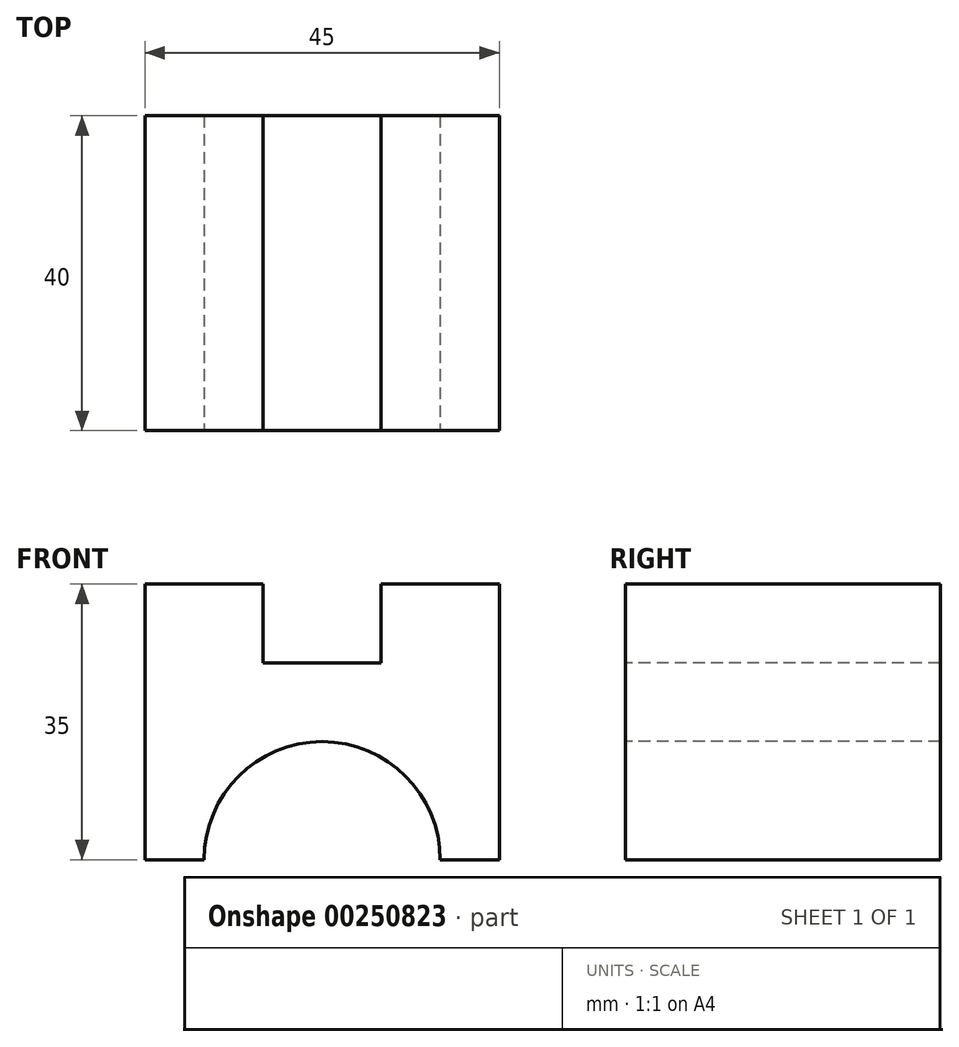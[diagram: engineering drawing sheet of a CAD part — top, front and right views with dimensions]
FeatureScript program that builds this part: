
annotation { "Feature Type Name" : "Feature", "Feature Type Description" : "" }
export const myFeature = defineFeature(function(context is Context, id is Id, definition is map)
    precondition{}
    {
        {
            var Q0;
            Q0=qCreatedBy(makeId("Top.planeOp"),FACE);
            var sketch = newSketch(context, id + "F0", { "sketchPlane" : qUnion([Q0])});
            skLineSegment(sketch, "E0", {"start": v(63.63, -20.93) * mm, "end": v(63.63, 19.07) * mm});
            skLineSegment(sketch, "E1", {"start": v(63.63, 19.07) * mm, "end": v(18.63, 19.07) * mm});
            skLineSegment(sketch, "E2", {"start": v(18.63, 19.07) * mm, "end": v(18.63, -20.93) * mm});
            skLineSegment(sketch, "E3", {"start": v(18.63, -20.93) * mm, "end": v(63.63, -20.93) * mm});
            skSolve(sketch);
        }
        {
            var Q0;
            Q0=qSketchRegion(id+"F0",true);
            extrude(context, id + "F1", {"entities" : qUnion([Q0]), "depth" : 25 * mm});
        }
        {
            var Q0;
            Q0=makeQuery(id+"F1.opExtrude","CAP_FACE",FACE,{"disambiguationData":[OSD([sQuery(id+"F0.wireOp",EDGE,"E0"),sQuery(id+"F0.wireOp",EDGE,"E1"),sQuery(id+"F0.wireOp",EDGE,"E2"),sQuery(id+"F0.wireOp",EDGE,"E3")])],"isStart":false});
            var sketch = newSketch(context, id + "F2", { "sketchPlane" : qUnion([Q0])});
            skLineSegment(sketch, "E4", {"start": v(48.63, 19.07) * mm, "end": v(48.63, -20.93) * mm});
            skLineSegment(sketch, "E5", {"start": v(33.63, 19.07) * mm, "end": v(33.63, -20.93) * mm});
            skSolve(sketch);
        }
        {
            var Q0;
            {var subQ0=sQuery(id+"F2.wireOp",EDGE,"E5");Q0=makeQuery(id+"F2.imprint","IMPRINT",FACE,{"disambiguationData":[TD([[makeQuery(id+"F2.imprint","IMPRINT",EDGE,{"derivedFrom":subQ0}),-1.0]])]});}
            var Q1;
            {var subQ0=sQuery(id+"F2.wireOp",EDGE,"E4");Q1=makeQuery(id+"F2.imprint","IMPRINT",FACE,{"disambiguationData":[TD([[makeQuery(id+"F2.imprint","IMPRINT",EDGE,{"derivedFrom":subQ0}),1.0]])]});}
            extrude(context, id + "F3", {"entities" : qUnion([Q0, Q1]), "operationType" : NewBodyOperationType.ADD, "depth" : 10 * mm});
        }
        {
            var Q0;
            {var subQ0=sQuery(id+"F0.wireOp",EDGE,"E3");var subQ1=makeQuery(id+"F1.opExtrude","CAP_EDGE",EDGE,{"disambiguationData":[OSD([subQ0])],"isStart":false});Q0=makeQuery(id+"F3.boolean.opBoolean","MERGE",FACE,{"derivedFrom":[makeQuery(id+"F1.opExtrude","SWEPT_FACE",FACE,{"disambiguationData":[OSD([subQ0])]}),makeQuery(id+"F3.opExtrude","SWEPT_FACE",FACE,{"disambiguationData":[OSD([subQ0]),TDD([makeQuery(id+"F2.imprint","IMPRINT",EDGE,{"disambiguationData":[TD([[makeQuery(id+"F2.imprint","INTERSECT",VERTEX,{"derivedFrom":[makeQuery(id+"F1.opExtrude","CAP_EDGE",EDGE,{"disambiguationData":[OSD([sQuery(id+"F0.wireOp",EDGE,"E0")])],"isStart":false}),subQ1]}),1.0]])],"derivedFrom":subQ1})])]}),makeQuery(id+"F3.opExtrude","SWEPT_FACE",FACE,{"disambiguationData":[OSD([subQ0]),TDD([makeQuery(id+"F2.imprint","IMPRINT",EDGE,{"disambiguationData":[TD([[makeQuery(id+"F2.imprint","INTERSECT",VERTEX,{"derivedFrom":[makeQuery(id+"F1.opExtrude","CAP_EDGE",EDGE,{"disambiguationData":[OSD([sQuery(id+"F0.wireOp",EDGE,"E2")])],"isStart":false}),subQ1]}),-1.0]])],"derivedFrom":subQ1})])]})]});}
            var sketch = newSketch(context, id + "F4", { "sketchPlane" : qUnion([Q0])});
            skArc(sketch, "E6", {"start": v(56.13, 0) * mm, "mid": v(41.13, 15) * mm, "end": v(26.13, 0) * mm});
            skLineSegment(sketch, "E7.0", {"start": v(26.13, 0) * mm, "end": v(56.13, 0) * mm});
            skPoint(sketch, "E8.orphan", {"position": v(18.63, 0) * mm});
            skPoint(sketch, "E9.orphan", {"position": v(63.63, 0) * mm});
            skSolve(sketch);
        }
        {
            var Q0;
            Q0=qSketchRegion(id+"F4",true);
            extrude(context, id + "F5", {"entities" : qUnion([Q0]), "operationType" : NewBodyOperationType.REMOVE, "endBound" : BoundingType.THROUGH_ALL, "oppositeDirection" : true, "depth" : 25.4 * mm});
        }
    });
